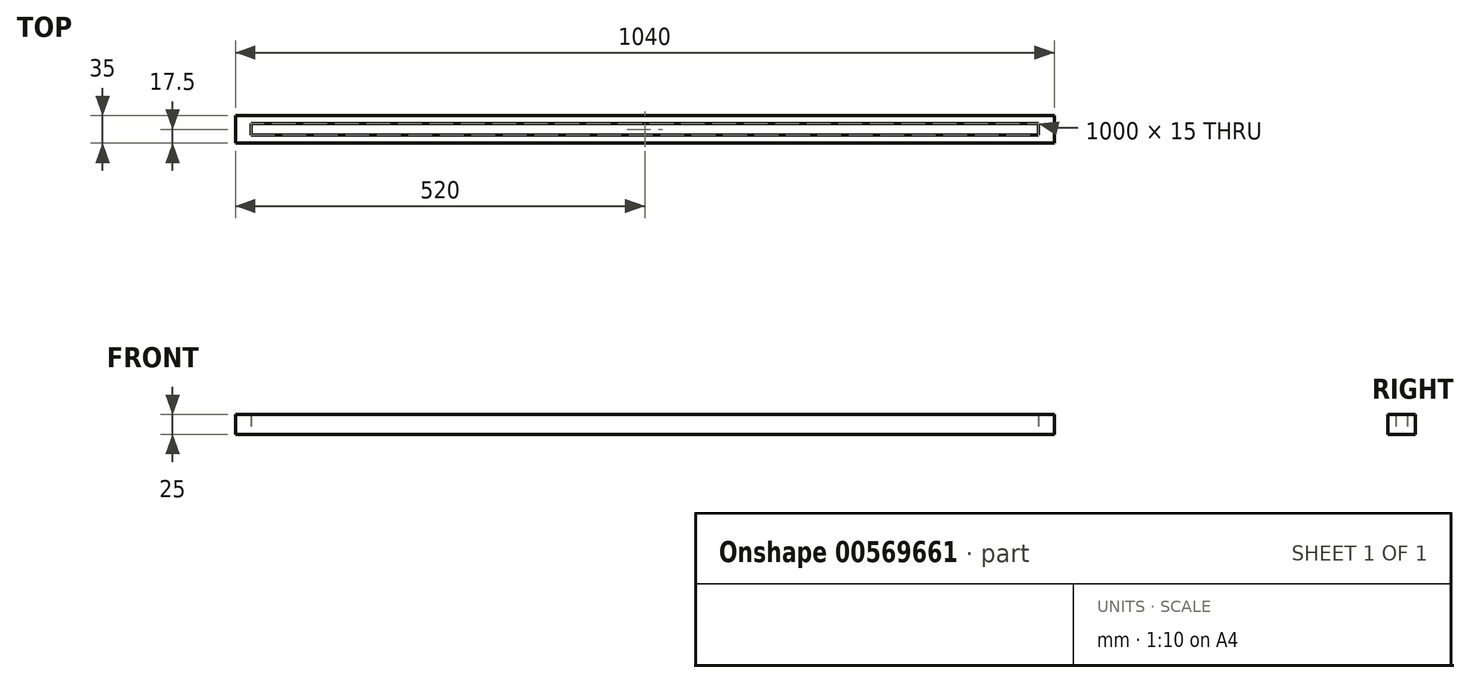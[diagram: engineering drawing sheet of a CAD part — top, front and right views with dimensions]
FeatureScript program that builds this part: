
annotation { "Feature Type Name" : "Feature", "Feature Type Description" : "" }
export const myFeature = defineFeature(function(context is Context, id is Id, definition is map)
    precondition{}
    {
        {
            var Q0;
            Q0=qCreatedBy(makeId("Front.planeOp"),FACE);
            var sketch = newSketch(context, id + "F0", { "sketchPlane" : qUnion([Q0])});
            skLineSegment(sketch, "E0.bottom", {"start": v(0, 0) * mm, "end": v(1040, 0) * mm});
            skLineSegment(sketch, "E0.top", {"start": v(0, 25) * mm, "end": v(1040, 25) * mm});
            skLineSegment(sketch, "E0.left", {"start": v(0, 0) * mm, "end": v(0, 25) * mm});
            skLineSegment(sketch, "E0.right", {"start": v(1040, 0) * mm, "end": v(1040, 25) * mm});
            skSolve(sketch);
        }
        {
            var Q0;
            Q0 = qSketchRegion(id + "F0", true);
            extrude(context, id + "F1", {"entities" : qUnion([Q0]), "depth" : 35 * mm, "offsetDistance" : 25 * mm});
        }
        {
            var Q0;
            Q0=makeQuery(id+"F1.opExtrude","SWEPT_FACE",FACE,{"disambiguationData":[OSD([sQuery(id+"F0.wireOp",EDGE,"E0.bottom")])]});
            var sketch = newSketch(context, id + "F2", { "sketchPlane" : qUnion([Q0])});
            skLineSegment(sketch, "E1.bottom", {"start": v(20, 25) * mm, "end": v(1020, 25) * mm});
            skLineSegment(sketch, "E1.top", {"start": v(20, 10) * mm, "end": v(1020, 10) * mm});
            skLineSegment(sketch, "E1.left", {"start": v(20, 25) * mm, "end": v(20, 10) * mm});
            skLineSegment(sketch, "E1.right", {"start": v(1020, 25) * mm, "end": v(1020, 10) * mm});
            skSolve(sketch);
        }
        {
            var Q0;
            Q0 = qSketchRegion(id + "F2", true);
            extrude(context, id + "F3", {"entities" : qUnion([Q0]), "operationType" : NewBodyOperationType.REMOVE, "endBound" : BoundingType.THROUGH_ALL, "oppositeDirection" : true, "depth" : 25 * mm, "offsetDistance" : 25 * mm});
        }
    });
